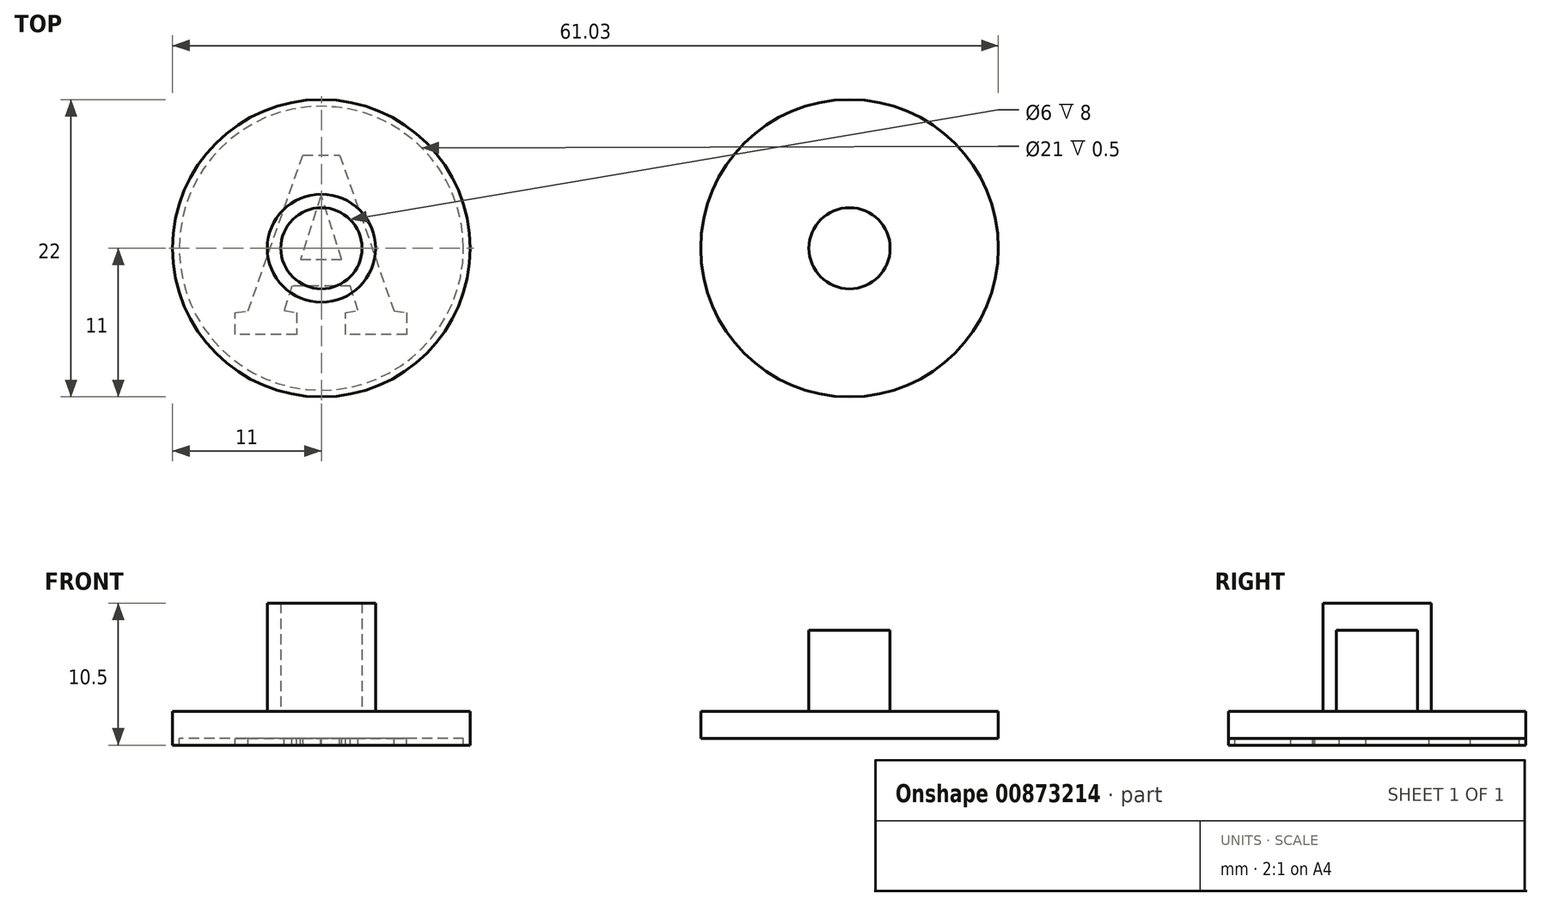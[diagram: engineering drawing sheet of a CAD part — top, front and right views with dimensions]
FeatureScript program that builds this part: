
annotation { "Feature Type Name" : "Feature", "Feature Type Description" : "" }
export const myFeature = defineFeature(function(context is Context, id is Id, definition is map)
    precondition{}
    {
        {
            var Q0;
            Q0=qCreatedBy(makeId("Top.planeOp"),FACE);
            var sketch = newSketch(context, id + "F0", { "sketchPlane" : qUnion([Q0])});
            skCircle(sketch, "E0", {"center": v(0, 0) * mm, "radius": 4 * mm});
            skCircle(sketch, "E1", {"center": v(0, 0) * mm, "radius": 11 * mm});
            skCircle(sketch, "E2", {"center": v(0, 0) * mm, "radius": 3 * mm});
            skSolve(sketch);
        }
        {
            var Q0;
            Q0=makeQuery(id+"F0.imprint","IMPRINT",FACE,{"disambiguationData":[TD([[makeQuery(id+"F0.imprint","IMPRINT",EDGE,{"derivedFrom":sQuery(id+"F0.wireOp",EDGE,"E0")}),-1.0]])]});
            extrude(context, id + "F1", {"entities" : qUnion([Q0]), "depth" : 2 * mm, "offsetDistance" : 25 * mm});
        }
        {
            var Q0;
            Q0=makeQuery(id+"F0.imprint","IMPRINT",FACE,{"disambiguationData":[TD([[makeQuery(id+"F0.imprint","IMPRINT",EDGE,{"derivedFrom":sQuery(id+"F0.wireOp",EDGE,"E0")}),1.0]])]});
            extrude(context, id + "F2", {"entities" : qUnion([Q0]), "operationType" : NewBodyOperationType.ADD, "depth" : 10 * mm, "offsetDistance" : 25 * mm});
        }
        {
            var Q0;
            Q0=makeQuery(id+"F0.imprint","IMPRINT",FACE,{"disambiguationData":[TD([[makeQuery(id+"F0.imprint","IMPRINT",EDGE,{"derivedFrom":sQuery(id+"F0.wireOp",EDGE,"E2")}),1.0]])]});
            extrude(context, id + "F3", {"entities" : qUnion([Q0]), "operationType" : NewBodyOperationType.ADD, "depth" : 2 * mm, "offsetDistance" : 25 * mm});
        }
        {
            var Q0;
            Q0=makeQuery(id+"F0.imprint","IMPRINT",FACE,{"disambiguationData":[TD([[makeQuery(id+"F0.imprint","IMPRINT",EDGE,{"derivedFrom":sQuery(id+"F0.wireOp",EDGE,"E0")}),-1.0]])]});
            var sketch = newSketch(context, id + "F4", { "sketchPlane" : qUnion([Q0])});
            skText(sketch, "E3", { "text": "A", "fontName": "RobotoSlab-Bold.ttf"});
            skCircle(sketch, "E4", {"center": v(0, 0) * mm, "radius": 11 * mm});
            skCircle(sketch, "E5", {"center": v(0, 0) * mm, "radius": 10.5 * mm});
            const initialGuessF4  = {"E3": [-0.00673, -0.00637, 1, 0, 0.01344]};
            skSetInitialGuess(sketch, initialGuessF4);
            skSolve(sketch);
        }
        {
            var Q0;
            Q0=makeQuery(id+"F4.imprint","IMPRINT",FACE,{"disambiguationData":[TD([[makeQuery(id+"F4.imprint","IMPRINT",EDGE,{"derivedFrom":sQuery(id+"F4.wireOp",EDGE,"E4")}),1.0]])]});
            var Q1;
            {var subQ6=sQuery(id+"F4.wireOp",EDGE,"E3.sketch_text.stroke-0");Q1=makeQuery(id+"F4.imprint","IMPRINT",FACE,{"disambiguationData":[TD([[makeQuery(id+"F4.imprint","IMPRINT",EDGE,{"derivedFrom":subQ6}),-1.0]])]});}
            var Q2;
            {var subQ5=sQuery(id+"F4.wireOp",EDGE,"E3.sketch_text.stroke-4");Q2=makeQuery(id+"F4.imprint","IMPRINT",FACE,{"disambiguationData":[TD([[makeQuery(id+"F4.imprint","IMPRINT",EDGE,{"derivedFrom":subQ5}),-1.0]])]});}
            var Q3;
            {var subQ8=sQuery(id+"F4.wireOp",EDGE,"E3.sketch_text.stroke-10");Q3=makeQuery(id+"F4.imprint","IMPRINT",FACE,{"disambiguationData":[TD([[makeQuery(id+"F4.imprint","IMPRINT",EDGE,{"derivedFrom":subQ8}),-1.0]])]});}
            var Q4;
            {var subQ0=sQuery(id+"F4.wireOp",EDGE,"E3.sketch_text.stroke-2");Q4=makeQuery(id+"F4.imprint","IMPRINT",FACE,{"disambiguationData":[TD([[makeQuery(id+"F4.imprint","IMPRINT",EDGE,{"derivedFrom":subQ0}),-1.0]])]});}
            extrude(context, id + "F5", {"entities" : qUnion([Q0, Q1, Q2, Q3, Q4]), "operationType" : NewBodyOperationType.ADD, "oppositeDirection" : true, "depth" : 0.5 * mm, "offsetDistance" : 25 * mm});
        }
        {
            var Q0;
            Q0=qCreatedBy(makeId("Top.planeOp"),FACE);
            var sketch = newSketch(context, id + "F6", { "sketchPlane" : qUnion([Q0])});
            skCircle(sketch, "E6", {"center": v(39.03, 0) * mm, "radius": 3 * mm});
            skCircle(sketch, "E7", {"center": v(39.03, 0) * mm, "radius": 11 * mm});
            skSolve(sketch);
        }
        {
            var Q0;
            Q0=makeQuery(id+"F6.imprint","IMPRINT",FACE,{"disambiguationData":[TD([[makeQuery(id+"F6.imprint","IMPRINT",EDGE,{"derivedFrom":sQuery(id+"F6.wireOp",EDGE,"E6")}),1.0]])]});
            extrude(context, id + "F7", {"entities" : qUnion([Q0]), "depth" : 8 * mm, "offsetDistance" : 25 * mm});
        }
        {
            var Q0;
            Q0=makeQuery(id+"F6.imprint","IMPRINT",FACE,{"disambiguationData":[TD([[makeQuery(id+"F6.imprint","IMPRINT",EDGE,{"derivedFrom":sQuery(id+"F6.wireOp",EDGE,"E6")}),-1.0]])]});
            extrude(context, id + "F8", {"entities" : qUnion([Q0]), "operationType" : NewBodyOperationType.ADD, "depth" : 2 * mm, "offsetDistance" : 25 * mm});
        }
    });
